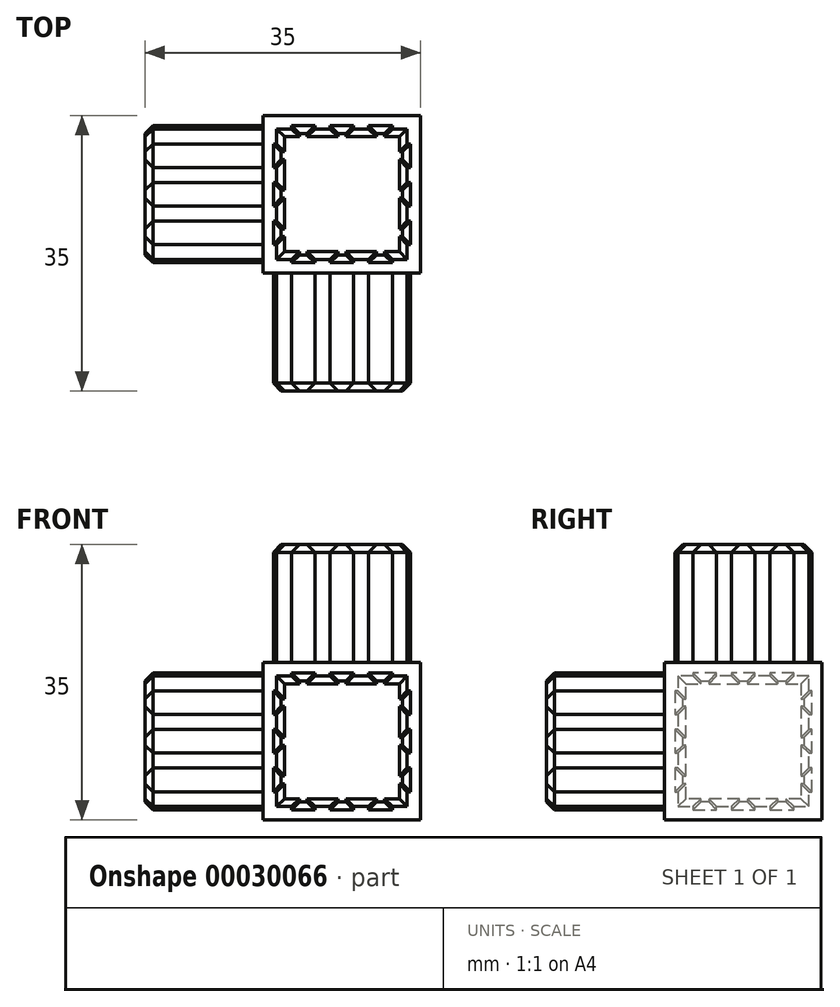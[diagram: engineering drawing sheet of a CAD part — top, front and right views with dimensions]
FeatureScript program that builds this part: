
annotation { "Feature Type Name" : "Feature", "Feature Type Description" : "" }
export const myFeature = defineFeature(function(context is Context, id is Id, definition is map)
    precondition{}
    {
        {
            var Q0;
            Q0=qCreatedBy(makeId("Top.planeOp"),FACE);
            var sketch = newSketch(context, id + "F0", { "sketchPlane" : qUnion([Q0])});
            skLineSegment(sketch, "E0", {"start": v(-8.3, 8.3) * mm, "end": v(-6.4, 8.3) * mm});
            skLineSegment(sketch, "E1", {"start": v(-6.4, 8.3) * mm, "end": v(-6.4, 8.7) * mm});
            skLineSegment(sketch, "E2", {"start": v(-6.4, 8.7) * mm, "end": v(-3.4, 8.7) * mm});
            skLineSegment(sketch, "E3", {"start": v(-3.4, 8.7) * mm, "end": v(-3.4, 8.3) * mm});
            skLineSegment(sketch, "E4", {"start": v(-3.4, 8.3) * mm, "end": v(-1.5, 8.3) * mm});
            skLineSegment(sketch, "E5", {"start": v(-1.5, 8.3) * mm, "end": v(-1.5, 8.7) * mm});
            skLineSegment(sketch, "E6", {"start": v(-1.5, 8.7) * mm, "end": v(1.5, 8.7) * mm});
            skLineSegment(sketch, "E7", {"start": v(1.5, 8.7) * mm, "end": v(1.5, 8.3) * mm});
            skLineSegment(sketch, "E8", {"start": v(1.5, 8.3) * mm, "end": v(3.4, 8.3) * mm});
            skLineSegment(sketch, "E9", {"start": v(3.4, 8.3) * mm, "end": v(3.4, 8.7) * mm});
            skLineSegment(sketch, "E10", {"start": v(3.4, 8.7) * mm, "end": v(6.4, 8.7) * mm});
            skLineSegment(sketch, "E11", {"start": v(6.4, 8.7) * mm, "end": v(6.4, 8.3) * mm});
            skLineSegment(sketch, "E12", {"start": v(6.4, 8.3) * mm, "end": v(8.3, 8.3) * mm});
            skLineSegment(sketch, "E13", {"start": v(-8.3, 8.3) * mm, "end": v(-8.3, 6.4) * mm});
            skLineSegment(sketch, "E14", {"start": v(-8.3, 6.4) * mm, "end": v(-8.7, 6.4) * mm});
            skLineSegment(sketch, "E15", {"start": v(-8.7, 6.4) * mm, "end": v(-8.7, 3.4) * mm});
            skLineSegment(sketch, "E16", {"start": v(-8.7, 3.4) * mm, "end": v(-8.3, 3.4) * mm});
            skLineSegment(sketch, "E17", {"start": v(-8.3, 3.4) * mm, "end": v(-8.3, 1.5) * mm});
            skLineSegment(sketch, "E18", {"start": v(-8.3, 1.5) * mm, "end": v(-8.7, 1.5) * mm});
            skLineSegment(sketch, "E19", {"start": v(-8.7, 1.5) * mm, "end": v(-8.7, -1.5) * mm});
            skLineSegment(sketch, "E20", {"start": v(-8.7, -1.5) * mm, "end": v(-8.3, -1.5) * mm});
            skLineSegment(sketch, "E21", {"start": v(-8.3, -1.5) * mm, "end": v(-8.3, -3.4) * mm});
            skLineSegment(sketch, "E22", {"start": v(-8.3, -3.4) * mm, "end": v(-8.7, -3.4) * mm});
            skLineSegment(sketch, "E23", {"start": v(-8.7, -3.4) * mm, "end": v(-8.7, -6.4) * mm});
            skLineSegment(sketch, "E24", {"start": v(-8.7, -6.4) * mm, "end": v(-8.3, -6.4) * mm});
            skLineSegment(sketch, "E25", {"start": v(-8.3, -6.4) * mm, "end": v(-8.3, -8.3) * mm});
            skLineSegment(sketch, "E26.MirrorCS", {"start": v(-6.4, -8.3) * mm, "end": v(-6.4, -8.7) * mm});
            skLineSegment(sketch, "E27.MirrorCS", {"start": v(-1.5, -8.3) * mm, "end": v(-1.5, -8.7) * mm});
            skLineSegment(sketch, "E28.MirrorCS", {"start": v(6.4, -8.7) * mm, "end": v(6.4, -8.3) * mm});
            skLineSegment(sketch, "E29.MirrorCS", {"start": v(1.5, -8.7) * mm, "end": v(1.5, -8.3) * mm});
            skLineSegment(sketch, "E30.MirrorCS", {"start": v(-3.4, -8.7) * mm, "end": v(-3.4, -8.3) * mm});
            skLineSegment(sketch, "E31.MirrorCS", {"start": v(3.4, -8.3) * mm, "end": v(3.4, -8.7) * mm});
            skLineSegment(sketch, "E32.MirrorCS", {"start": v(-8.3, -8.3) * mm, "end": v(-6.4, -8.3) * mm});
            skLineSegment(sketch, "E33.MirrorCS", {"start": v(-3.4, -8.3) * mm, "end": v(-1.5, -8.3) * mm});
            skLineSegment(sketch, "E34.MirrorCS", {"start": v(-1.5, -8.7) * mm, "end": v(1.5, -8.7) * mm});
            skLineSegment(sketch, "E35.MirrorCS", {"start": v(6.4, -8.3) * mm, "end": v(8.3, -8.3) * mm});
            skLineSegment(sketch, "E36.MirrorCS", {"start": v(-6.4, -8.7) * mm, "end": v(-3.4, -8.7) * mm});
            skLineSegment(sketch, "E37.MirrorCS", {"start": v(1.5, -8.3) * mm, "end": v(3.4, -8.3) * mm});
            skLineSegment(sketch, "E38.MirrorCS", {"start": v(3.4, -8.7) * mm, "end": v(6.4, -8.7) * mm});
            skLineSegment(sketch, "E39.MirrorCS", {"start": v(8.3, 6.4) * mm, "end": v(8.7, 6.4) * mm});
            skLineSegment(sketch, "E40.MirrorCS", {"start": v(8.3, 1.5) * mm, "end": v(8.7, 1.5) * mm});
            skLineSegment(sketch, "E41.MirrorCS", {"start": v(8.7, -6.4) * mm, "end": v(8.3, -6.4) * mm});
            skLineSegment(sketch, "E42.MirrorCS", {"start": v(8.7, -1.5) * mm, "end": v(8.3, -1.5) * mm});
            skLineSegment(sketch, "E43.MirrorCS", {"start": v(8.3, -3.4) * mm, "end": v(8.7, -3.4) * mm});
            skLineSegment(sketch, "E44.MirrorCS", {"start": v(8.7, 3.4) * mm, "end": v(8.3, 3.4) * mm});
            skLineSegment(sketch, "E45.MirrorCS", {"start": v(8.7, -3.4) * mm, "end": v(8.7, -6.4) * mm});
            skLineSegment(sketch, "E46.MirrorCS", {"start": v(8.3, 8.3) * mm, "end": v(8.3, 6.4) * mm});
            skLineSegment(sketch, "E47.MirrorCS", {"start": v(8.7, 6.4) * mm, "end": v(8.7, 3.4) * mm});
            skLineSegment(sketch, "E48.MirrorCS", {"start": v(8.3, -1.5) * mm, "end": v(8.3, -3.4) * mm});
            skLineSegment(sketch, "E49.MirrorCS", {"start": v(8.7, 1.5) * mm, "end": v(8.7, -1.5) * mm});
            skLineSegment(sketch, "E50.MirrorCS", {"start": v(8.3, 3.4) * mm, "end": v(8.3, 1.5) * mm});
            skLineSegment(sketch, "E51.MirrorCS", {"start": v(8.3, -6.4) * mm, "end": v(8.3, -8.3) * mm});
            skLineSegment(sketch, "E52.rect.bottom", {"start": v(10, 10) * mm, "end": v(-10, 10) * mm});
            skLineSegment(sketch, "E52.rect.top", {"start": v(10, -10) * mm, "end": v(-10, -10) * mm});
            skLineSegment(sketch, "E52.rect.left", {"start": v(10, 10) * mm, "end": v(10, -10) * mm});
            skLineSegment(sketch, "E52.rect.right", {"start": v(-10, 10) * mm, "end": v(-10, -10) * mm});
            skPoint(sketch, "E52.rect.middle", {"position": v(0, 0) * mm});
            skSolve(sketch);
        }
        {
            var Q0;
            Q0=makeQuery(id+"F0.imprint","IMPRINT",FACE,{"disambiguationData":[TD([[makeQuery(id+"F0.imprint","IMPRINT",EDGE,{"derivedFrom":sQuery(id+"F0.wireOp",EDGE,"E0")}),1.0]])]});
            var Q1;
            Q1=makeQuery(id+"F0.imprint","IMPRINT",FACE,{"disambiguationData":[TD([[makeQuery(id+"F0.imprint","IMPRINT",EDGE,{"derivedFrom":sQuery(id+"F0.wireOp",EDGE,"E0")}),-1.0]])]});
            var Q2;
            Q2=makeQuery(id+"F0.imprint","IMPRINT",FACE,{"disambiguationData":[TD([[makeQuery(id+"F0.imprint","IMPRINT",EDGE,{"derivedFrom":sQuery(id+"F0.wireOp",EDGE,"E0")}),-1.0]])]});
            extrude(context, id + "F1", {"entities" : qUnion([Q0, Q1, Q2]), "oppositeDirection" : true, "depth" : 20 * mm});
        }
        {
            var Q0;
            Q0=makeQuery(id+"F0.imprint","IMPRINT",FACE,{"disambiguationData":[TD([[makeQuery(id+"F0.imprint","IMPRINT",EDGE,{"derivedFrom":sQuery(id+"F0.wireOp",EDGE,"E0")}),-1.0]])]});
            extrude(context, id + "F2", {"entities" : qUnion([Q0]), "depth" : 15 * mm});
        }
        {
            var Q0;
            Q0=makeQuery(id+"F2.opExtrude","CAP_FACE",FACE,{"disambiguationData":[OSD([sQuery(id+"F0.wireOp",EDGE,"E0"),sQuery(id+"F0.wireOp",EDGE,"E1"),sQuery(id+"F0.wireOp",EDGE,"E2"),sQuery(id+"F0.wireOp",EDGE,"E3"),sQuery(id+"F0.wireOp",EDGE,"E4"),sQuery(id+"F0.wireOp",EDGE,"E5"),sQuery(id+"F0.wireOp",EDGE,"E6"),sQuery(id+"F0.wireOp",EDGE,"E7"),sQuery(id+"F0.wireOp",EDGE,"E8"),sQuery(id+"F0.wireOp",EDGE,"E9"),sQuery(id+"F0.wireOp",EDGE,"E10"),sQuery(id+"F0.wireOp",EDGE,"E11"),sQuery(id+"F0.wireOp",EDGE,"E12"),sQuery(id+"F0.wireOp",EDGE,"E13"),sQuery(id+"F0.wireOp",EDGE,"E14"),sQuery(id+"F0.wireOp",EDGE,"E15"),sQuery(id+"F0.wireOp",EDGE,"E16"),sQuery(id+"F0.wireOp",EDGE,"E17"),sQuery(id+"F0.wireOp",EDGE,"E18"),sQuery(id+"F0.wireOp",EDGE,"E19"),sQuery(id+"F0.wireOp",EDGE,"E20"),sQuery(id+"F0.wireOp",EDGE,"E21"),sQuery(id+"F0.wireOp",EDGE,"E22"),sQuery(id+"F0.wireOp",EDGE,"E23"),sQuery(id+"F0.wireOp",EDGE,"E24"),sQuery(id+"F0.wireOp",EDGE,"E25"),sQuery(id+"F0.wireOp",EDGE,"E26.MirrorCS"),sQuery(id+"F0.wireOp",EDGE,"E27.MirrorCS"),sQuery(id+"F0.wireOp",EDGE,"E28.MirrorCS"),sQuery(id+"F0.wireOp",EDGE,"E29.MirrorCS"),sQuery(id+"F0.wireOp",EDGE,"E30.MirrorCS"),sQuery(id+"F0.wireOp",EDGE,"E31.MirrorCS"),sQuery(id+"F0.wireOp",EDGE,"E32.MirrorCS"),sQuery(id+"F0.wireOp",EDGE,"E33.MirrorCS"),sQuery(id+"F0.wireOp",EDGE,"E34.MirrorCS"),sQuery(id+"F0.wireOp",EDGE,"E35.MirrorCS"),sQuery(id+"F0.wireOp",EDGE,"E36.MirrorCS"),sQuery(id+"F0.wireOp",EDGE,"E37.MirrorCS"),sQuery(id+"F0.wireOp",EDGE,"E38.MirrorCS"),sQuery(id+"F0.wireOp",EDGE,"E39.MirrorCS"),sQuery(id+"F0.wireOp",EDGE,"E40.MirrorCS"),sQuery(id+"F0.wireOp",EDGE,"E41.MirrorCS"),sQuery(id+"F0.wireOp",EDGE,"E42.MirrorCS"),sQuery(id+"F0.wireOp",EDGE,"E43.MirrorCS"),sQuery(id+"F0.wireOp",EDGE,"E44.MirrorCS"),sQuery(id+"F0.wireOp",EDGE,"E45.MirrorCS"),sQuery(id+"F0.wireOp",EDGE,"E46.MirrorCS"),sQuery(id+"F0.wireOp",EDGE,"E47.MirrorCS"),sQuery(id+"F0.wireOp",EDGE,"E48.MirrorCS"),sQuery(id+"F0.wireOp",EDGE,"E49.MirrorCS"),sQuery(id+"F0.wireOp",EDGE,"E50.MirrorCS"),sQuery(id+"F0.wireOp",EDGE,"E51.MirrorCS")])],"isStart":false});
            chamfer(context, id + "F3", {"entities" : qUnion([Q0]), "width" : 1 * mm, "tangentPropagation" : true});
        }
        {
            var Q0;
            Q0=makeQuery(id+"F2.opExtrude","SWEPT_BODY",BODY,{"disambiguationData":[OSD([sQuery(id+"F0.wireOp",EDGE,"E0"),sQuery(id+"F0.wireOp",EDGE,"E1"),sQuery(id+"F0.wireOp",EDGE,"E2"),sQuery(id+"F0.wireOp",EDGE,"E3"),sQuery(id+"F0.wireOp",EDGE,"E4"),sQuery(id+"F0.wireOp",EDGE,"E5"),sQuery(id+"F0.wireOp",EDGE,"E6"),sQuery(id+"F0.wireOp",EDGE,"E7"),sQuery(id+"F0.wireOp",EDGE,"E8"),sQuery(id+"F0.wireOp",EDGE,"E9"),sQuery(id+"F0.wireOp",EDGE,"E10"),sQuery(id+"F0.wireOp",EDGE,"E11"),sQuery(id+"F0.wireOp",EDGE,"E12"),sQuery(id+"F0.wireOp",EDGE,"E13"),sQuery(id+"F0.wireOp",EDGE,"E14"),sQuery(id+"F0.wireOp",EDGE,"E15"),sQuery(id+"F0.wireOp",EDGE,"E16"),sQuery(id+"F0.wireOp",EDGE,"E17"),sQuery(id+"F0.wireOp",EDGE,"E18"),sQuery(id+"F0.wireOp",EDGE,"E19"),sQuery(id+"F0.wireOp",EDGE,"E20"),sQuery(id+"F0.wireOp",EDGE,"E21"),sQuery(id+"F0.wireOp",EDGE,"E22"),sQuery(id+"F0.wireOp",EDGE,"E23"),sQuery(id+"F0.wireOp",EDGE,"E24"),sQuery(id+"F0.wireOp",EDGE,"E25"),sQuery(id+"F0.wireOp",EDGE,"E26.MirrorCS"),sQuery(id+"F0.wireOp",EDGE,"E27.MirrorCS"),sQuery(id+"F0.wireOp",EDGE,"E28.MirrorCS"),sQuery(id+"F0.wireOp",EDGE,"E29.MirrorCS"),sQuery(id+"F0.wireOp",EDGE,"E30.MirrorCS"),sQuery(id+"F0.wireOp",EDGE,"E31.MirrorCS"),sQuery(id+"F0.wireOp",EDGE,"E32.MirrorCS"),sQuery(id+"F0.wireOp",EDGE,"E33.MirrorCS"),sQuery(id+"F0.wireOp",EDGE,"E34.MirrorCS"),sQuery(id+"F0.wireOp",EDGE,"E35.MirrorCS"),sQuery(id+"F0.wireOp",EDGE,"E36.MirrorCS"),sQuery(id+"F0.wireOp",EDGE,"E37.MirrorCS"),sQuery(id+"F0.wireOp",EDGE,"E38.MirrorCS"),sQuery(id+"F0.wireOp",EDGE,"E39.MirrorCS"),sQuery(id+"F0.wireOp",EDGE,"E40.MirrorCS"),sQuery(id+"F0.wireOp",EDGE,"E41.MirrorCS"),sQuery(id+"F0.wireOp",EDGE,"E42.MirrorCS"),sQuery(id+"F0.wireOp",EDGE,"E43.MirrorCS"),sQuery(id+"F0.wireOp",EDGE,"E44.MirrorCS"),sQuery(id+"F0.wireOp",EDGE,"E45.MirrorCS"),sQuery(id+"F0.wireOp",EDGE,"E46.MirrorCS"),sQuery(id+"F0.wireOp",EDGE,"E47.MirrorCS"),sQuery(id+"F0.wireOp",EDGE,"E48.MirrorCS"),sQuery(id+"F0.wireOp",EDGE,"E49.MirrorCS"),sQuery(id+"F0.wireOp",EDGE,"E50.MirrorCS"),sQuery(id+"F0.wireOp",EDGE,"E51.MirrorCS")])]});
            var Q1;
            Q1=sQuery(id+"F0.wireOp",EDGE,"E52.rect.left");
            transform(context, id + "F4", {"entities" : qUnion([Q0]), "transformType" : TransformType.ROTATION, "transformAxis" : qUnion([Q1]), "angle" : 90 * degree, "makeCopy" : true});
        }
        {
            var Q0;
            Q0=makeQuery(id+"F4.opPattern","COPY",BODY,{"derivedFrom":makeQuery(id+"F2.opExtrude","SWEPT_BODY",BODY,{"disambiguationData":[OSD([sQuery(id+"F0.wireOp",EDGE,"E0"),sQuery(id+"F0.wireOp",EDGE,"E1"),sQuery(id+"F0.wireOp",EDGE,"E2"),sQuery(id+"F0.wireOp",EDGE,"E3"),sQuery(id+"F0.wireOp",EDGE,"E4"),sQuery(id+"F0.wireOp",EDGE,"E5"),sQuery(id+"F0.wireOp",EDGE,"E6"),sQuery(id+"F0.wireOp",EDGE,"E7"),sQuery(id+"F0.wireOp",EDGE,"E8"),sQuery(id+"F0.wireOp",EDGE,"E9"),sQuery(id+"F0.wireOp",EDGE,"E10"),sQuery(id+"F0.wireOp",EDGE,"E11"),sQuery(id+"F0.wireOp",EDGE,"E12"),sQuery(id+"F0.wireOp",EDGE,"E13"),sQuery(id+"F0.wireOp",EDGE,"E14"),sQuery(id+"F0.wireOp",EDGE,"E15"),sQuery(id+"F0.wireOp",EDGE,"E16"),sQuery(id+"F0.wireOp",EDGE,"E17"),sQuery(id+"F0.wireOp",EDGE,"E18"),sQuery(id+"F0.wireOp",EDGE,"E19"),sQuery(id+"F0.wireOp",EDGE,"E20"),sQuery(id+"F0.wireOp",EDGE,"E21"),sQuery(id+"F0.wireOp",EDGE,"E22"),sQuery(id+"F0.wireOp",EDGE,"E23"),sQuery(id+"F0.wireOp",EDGE,"E24"),sQuery(id+"F0.wireOp",EDGE,"E25"),sQuery(id+"F0.wireOp",EDGE,"E26.MirrorCS"),sQuery(id+"F0.wireOp",EDGE,"E27.MirrorCS"),sQuery(id+"F0.wireOp",EDGE,"E28.MirrorCS"),sQuery(id+"F0.wireOp",EDGE,"E29.MirrorCS"),sQuery(id+"F0.wireOp",EDGE,"E30.MirrorCS"),sQuery(id+"F0.wireOp",EDGE,"E31.MirrorCS"),sQuery(id+"F0.wireOp",EDGE,"E32.MirrorCS"),sQuery(id+"F0.wireOp",EDGE,"E33.MirrorCS"),sQuery(id+"F0.wireOp",EDGE,"E34.MirrorCS"),sQuery(id+"F0.wireOp",EDGE,"E35.MirrorCS"),sQuery(id+"F0.wireOp",EDGE,"E36.MirrorCS"),sQuery(id+"F0.wireOp",EDGE,"E37.MirrorCS"),sQuery(id+"F0.wireOp",EDGE,"E38.MirrorCS"),sQuery(id+"F0.wireOp",EDGE,"E39.MirrorCS"),sQuery(id+"F0.wireOp",EDGE,"E40.MirrorCS"),sQuery(id+"F0.wireOp",EDGE,"E41.MirrorCS"),sQuery(id+"F0.wireOp",EDGE,"E42.MirrorCS"),sQuery(id+"F0.wireOp",EDGE,"E43.MirrorCS"),sQuery(id+"F0.wireOp",EDGE,"E44.MirrorCS"),sQuery(id+"F0.wireOp",EDGE,"E45.MirrorCS"),sQuery(id+"F0.wireOp",EDGE,"E46.MirrorCS"),sQuery(id+"F0.wireOp",EDGE,"E47.MirrorCS"),sQuery(id+"F0.wireOp",EDGE,"E48.MirrorCS"),sQuery(id+"F0.wireOp",EDGE,"E49.MirrorCS"),sQuery(id+"F0.wireOp",EDGE,"E50.MirrorCS"),sQuery(id+"F0.wireOp",EDGE,"E51.MirrorCS")])]}),"instanceName":"1"});
            var Q1;
            Q1=sQuery(id+"F0.wireOp",EDGE,"E52.rect.top");
            transform(context, id + "F5", {"entities" : qUnion([Q0]), "transformType" : TransformType.TRANSLATION_ENTITY, "oppositeDirectionEntity" : false, "transformLine" : qUnion([Q1]), "makeCopy" : false});
        }
        {
            var Q0;
            Q0=makeQuery(id+"F4.opPattern","COPY",BODY,{"derivedFrom":makeQuery(id+"F2.opExtrude","SWEPT_BODY",BODY,{"disambiguationData":[OSD([sQuery(id+"F0.wireOp",EDGE,"E0"),sQuery(id+"F0.wireOp",EDGE,"E1"),sQuery(id+"F0.wireOp",EDGE,"E2"),sQuery(id+"F0.wireOp",EDGE,"E3"),sQuery(id+"F0.wireOp",EDGE,"E4"),sQuery(id+"F0.wireOp",EDGE,"E5"),sQuery(id+"F0.wireOp",EDGE,"E6"),sQuery(id+"F0.wireOp",EDGE,"E7"),sQuery(id+"F0.wireOp",EDGE,"E8"),sQuery(id+"F0.wireOp",EDGE,"E9"),sQuery(id+"F0.wireOp",EDGE,"E10"),sQuery(id+"F0.wireOp",EDGE,"E11"),sQuery(id+"F0.wireOp",EDGE,"E12"),sQuery(id+"F0.wireOp",EDGE,"E13"),sQuery(id+"F0.wireOp",EDGE,"E14"),sQuery(id+"F0.wireOp",EDGE,"E15"),sQuery(id+"F0.wireOp",EDGE,"E16"),sQuery(id+"F0.wireOp",EDGE,"E17"),sQuery(id+"F0.wireOp",EDGE,"E18"),sQuery(id+"F0.wireOp",EDGE,"E19"),sQuery(id+"F0.wireOp",EDGE,"E20"),sQuery(id+"F0.wireOp",EDGE,"E21"),sQuery(id+"F0.wireOp",EDGE,"E22"),sQuery(id+"F0.wireOp",EDGE,"E23"),sQuery(id+"F0.wireOp",EDGE,"E24"),sQuery(id+"F0.wireOp",EDGE,"E25"),sQuery(id+"F0.wireOp",EDGE,"E26.MirrorCS"),sQuery(id+"F0.wireOp",EDGE,"E27.MirrorCS"),sQuery(id+"F0.wireOp",EDGE,"E28.MirrorCS"),sQuery(id+"F0.wireOp",EDGE,"E29.MirrorCS"),sQuery(id+"F0.wireOp",EDGE,"E30.MirrorCS"),sQuery(id+"F0.wireOp",EDGE,"E31.MirrorCS"),sQuery(id+"F0.wireOp",EDGE,"E32.MirrorCS"),sQuery(id+"F0.wireOp",EDGE,"E33.MirrorCS"),sQuery(id+"F0.wireOp",EDGE,"E34.MirrorCS"),sQuery(id+"F0.wireOp",EDGE,"E35.MirrorCS"),sQuery(id+"F0.wireOp",EDGE,"E36.MirrorCS"),sQuery(id+"F0.wireOp",EDGE,"E37.MirrorCS"),sQuery(id+"F0.wireOp",EDGE,"E38.MirrorCS"),sQuery(id+"F0.wireOp",EDGE,"E39.MirrorCS"),sQuery(id+"F0.wireOp",EDGE,"E40.MirrorCS"),sQuery(id+"F0.wireOp",EDGE,"E41.MirrorCS"),sQuery(id+"F0.wireOp",EDGE,"E42.MirrorCS"),sQuery(id+"F0.wireOp",EDGE,"E43.MirrorCS"),sQuery(id+"F0.wireOp",EDGE,"E44.MirrorCS"),sQuery(id+"F0.wireOp",EDGE,"E45.MirrorCS"),sQuery(id+"F0.wireOp",EDGE,"E46.MirrorCS"),sQuery(id+"F0.wireOp",EDGE,"E47.MirrorCS"),sQuery(id+"F0.wireOp",EDGE,"E48.MirrorCS"),sQuery(id+"F0.wireOp",EDGE,"E49.MirrorCS"),sQuery(id+"F0.wireOp",EDGE,"E50.MirrorCS"),sQuery(id+"F0.wireOp",EDGE,"E51.MirrorCS")])]}),"instanceName":"1"});
            var Q1;
            Q1=makeQuery(id+"F1.opExtrude","SWEPT_EDGE",EDGE,{"disambiguationData":[OSD([sQuery(id+"F0.wireOp",EDGE,"E52.rect.bottom"),sQuery(id+"F0.wireOp",EDGE,"E52.rect.right")])]});
            transform(context, id + "F6", {"entities" : qUnion([Q0]), "transformType" : TransformType.ROTATION, "transformAxis" : qUnion([Q1]), "angle" : 90 * degree, "makeCopy" : true});
        }
        {
            var Q0;
            Q0=makeQuery(id+"F6.opPattern","COPY",BODY,{"derivedFrom":makeQuery(id+"F4.opPattern","COPY",BODY,{"derivedFrom":makeQuery(id+"F2.opExtrude","SWEPT_BODY",BODY,{"disambiguationData":[OSD([sQuery(id+"F0.wireOp",EDGE,"E0"),sQuery(id+"F0.wireOp",EDGE,"E1"),sQuery(id+"F0.wireOp",EDGE,"E2"),sQuery(id+"F0.wireOp",EDGE,"E3"),sQuery(id+"F0.wireOp",EDGE,"E4"),sQuery(id+"F0.wireOp",EDGE,"E5"),sQuery(id+"F0.wireOp",EDGE,"E6"),sQuery(id+"F0.wireOp",EDGE,"E7"),sQuery(id+"F0.wireOp",EDGE,"E8"),sQuery(id+"F0.wireOp",EDGE,"E9"),sQuery(id+"F0.wireOp",EDGE,"E10"),sQuery(id+"F0.wireOp",EDGE,"E11"),sQuery(id+"F0.wireOp",EDGE,"E12"),sQuery(id+"F0.wireOp",EDGE,"E13"),sQuery(id+"F0.wireOp",EDGE,"E14"),sQuery(id+"F0.wireOp",EDGE,"E15"),sQuery(id+"F0.wireOp",EDGE,"E16"),sQuery(id+"F0.wireOp",EDGE,"E17"),sQuery(id+"F0.wireOp",EDGE,"E18"),sQuery(id+"F0.wireOp",EDGE,"E19"),sQuery(id+"F0.wireOp",EDGE,"E20"),sQuery(id+"F0.wireOp",EDGE,"E21"),sQuery(id+"F0.wireOp",EDGE,"E22"),sQuery(id+"F0.wireOp",EDGE,"E23"),sQuery(id+"F0.wireOp",EDGE,"E24"),sQuery(id+"F0.wireOp",EDGE,"E25"),sQuery(id+"F0.wireOp",EDGE,"E26.MirrorCS"),sQuery(id+"F0.wireOp",EDGE,"E27.MirrorCS"),sQuery(id+"F0.wireOp",EDGE,"E28.MirrorCS"),sQuery(id+"F0.wireOp",EDGE,"E29.MirrorCS"),sQuery(id+"F0.wireOp",EDGE,"E30.MirrorCS"),sQuery(id+"F0.wireOp",EDGE,"E31.MirrorCS"),sQuery(id+"F0.wireOp",EDGE,"E32.MirrorCS"),sQuery(id+"F0.wireOp",EDGE,"E33.MirrorCS"),sQuery(id+"F0.wireOp",EDGE,"E34.MirrorCS"),sQuery(id+"F0.wireOp",EDGE,"E35.MirrorCS"),sQuery(id+"F0.wireOp",EDGE,"E36.MirrorCS"),sQuery(id+"F0.wireOp",EDGE,"E37.MirrorCS"),sQuery(id+"F0.wireOp",EDGE,"E38.MirrorCS"),sQuery(id+"F0.wireOp",EDGE,"E39.MirrorCS"),sQuery(id+"F0.wireOp",EDGE,"E40.MirrorCS"),sQuery(id+"F0.wireOp",EDGE,"E41.MirrorCS"),sQuery(id+"F0.wireOp",EDGE,"E42.MirrorCS"),sQuery(id+"F0.wireOp",EDGE,"E43.MirrorCS"),sQuery(id+"F0.wireOp",EDGE,"E44.MirrorCS"),sQuery(id+"F0.wireOp",EDGE,"E45.MirrorCS"),sQuery(id+"F0.wireOp",EDGE,"E46.MirrorCS"),sQuery(id+"F0.wireOp",EDGE,"E47.MirrorCS"),sQuery(id+"F0.wireOp",EDGE,"E48.MirrorCS"),sQuery(id+"F0.wireOp",EDGE,"E49.MirrorCS"),sQuery(id+"F0.wireOp",EDGE,"E50.MirrorCS"),sQuery(id+"F0.wireOp",EDGE,"E51.MirrorCS")])]}),"instanceName":"1"}),"instanceName":"1"});
            var Q1;
            Q1=makeQuery(id+"F1.opExtrude","CAP_EDGE",EDGE,{"disambiguationData":[OSD([sQuery(id+"F0.wireOp",EDGE,"E52.rect.right")])],"isStart":true});
            transform(context, id + "F7", {"entities" : qUnion([Q0]), "transformType" : TransformType.TRANSLATION_ENTITY, "oppositeDirectionEntity" : false, "transformLine" : qUnion([Q1]), "makeCopy" : false});
        }
    });
